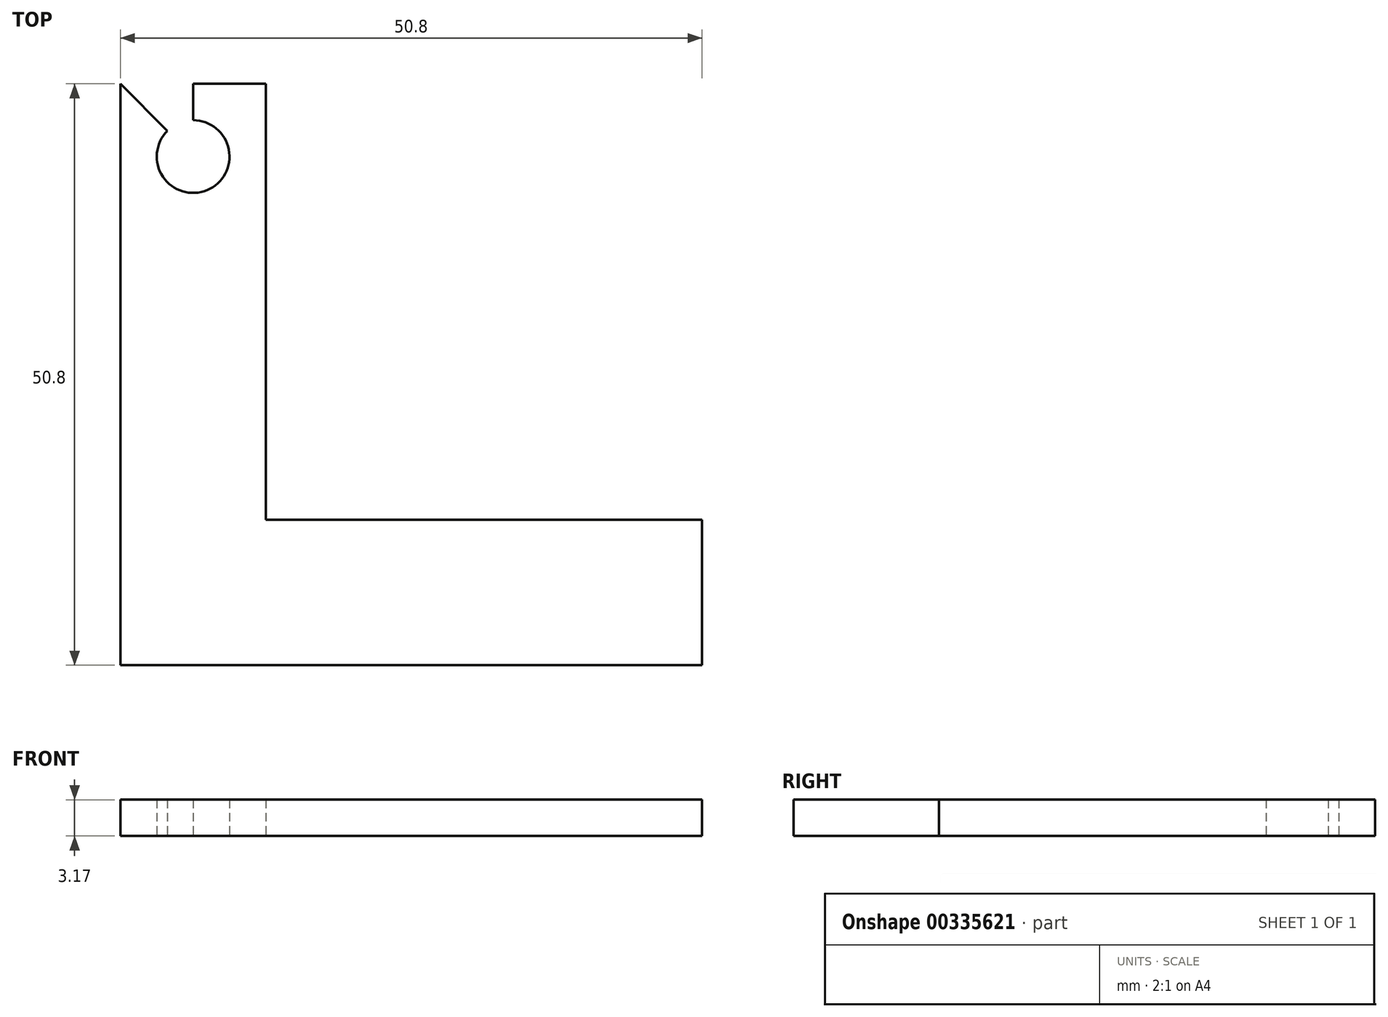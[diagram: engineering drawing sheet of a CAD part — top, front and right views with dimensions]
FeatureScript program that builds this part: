
annotation { "Feature Type Name" : "Feature", "Feature Type Description" : "" }
export const myFeature = defineFeature(function(context is Context, id is Id, definition is map)
    precondition{}
    {
        {
            var Q0;
            Q0=qCreatedBy(makeId("Top.planeOp"),FACE);
            var sketch = newSketch(context, id + "F0", { "sketchPlane" : qUnion([Q0])});
            skLineSegment(sketch, "E0.bottom", {"start": v(0, 50.8) * mm, "end": v(12.7, 50.8) * mm});
            skLineSegment(sketch, "E0.top", {"start": v(0, 0) * mm, "end": v(12.7, 0) * mm});
            skLineSegment(sketch, "E0.left", {"start": v(0, 50.8) * mm, "end": v(0, 0) * mm});
            skLineSegment(sketch, "E0.right", {"start": v(12.7, 50.8) * mm, "end": v(12.7, 0) * mm});
            skLineSegment(sketch, "E1.bottom", {"start": v(12.7, 0) * mm, "end": v(50.8, 0) * mm});
            skLineSegment(sketch, "E1.top", {"start": v(12.7, 12.7) * mm, "end": v(50.8, 12.7) * mm});
            skLineSegment(sketch, "E1.left", {"start": v(12.7, 0) * mm, "end": v(12.7, 12.7) * mm});
            skLineSegment(sketch, "E1.right", {"start": v(50.8, 0) * mm, "end": v(50.8, 12.7) * mm});
            skLineSegment(sketch, "E2.bottom", {"start": v(50.8, 12.7) * mm, "end": v(38.1, 12.7) * mm});
            skLineSegment(sketch, "E2.top", {"start": v(50.8, 25.4) * mm, "end": v(38.1, 25.4) * mm});
            skLineSegment(sketch, "E2.left", {"start": v(50.8, 12.7) * mm, "end": v(50.8, 25.4) * mm});
            skLineSegment(sketch, "E2.right", {"start": v(38.1, 12.7) * mm, "end": v(38.1, 25.4) * mm});
            skLineSegment(sketch, "E3", {"start": v(0, 50.8) * mm, "end": v(60.58, -9.78) * mm});
            skCircle(sketch, "E4", {"center": v(6.35, 44.45) * mm, "radius": 3.18 * mm});
            skLineSegment(sketch, "E5", {"start": v(6.35, 50.8) * mm, "end": v(6.35, 44.45) * mm});
            skSolve(sketch);
        }
        {
            var Q0;
            Q0=makeQuery(id+"F0.imprint","IMPRINT",FACE,{"disambiguationData":[TD([[makeQuery(id+"F0.imprint","IMPRINT",EDGE,{"derivedFrom":sQuery(id+"F0.wireOp",EDGE,"E2.bottom")}),-1.0]])]});
            var Q1;
            {var subQ0=sQuery(id+"F0.wireOp",EDGE,"E1.right");Q1=makeQuery(id+"F0.imprint","IMPRINT",FACE,{"disambiguationData":[TD([[makeQuery(id+"F0.imprint","IMPRINT",EDGE,{"derivedFrom":subQ0}),1.0]])]});}
            var Q2;
            {var subQ0=sQuery(id+"F0.wireOp",EDGE,"E1.bottom");Q2=makeQuery(id+"F0.imprint","IMPRINT",FACE,{"disambiguationData":[TD([[makeQuery(id+"F0.imprint","IMPRINT",EDGE,{"derivedFrom":subQ0}),1.0]])]});}
            var Q3;
            Q3=makeQuery(id+"F0.imprint","IMPRINT",FACE,{"disambiguationData":[TD([[makeQuery(id+"F0.imprint","IMPRINT",EDGE,{"derivedFrom":sQuery(id+"F0.wireOp",EDGE,"E0.top")}),1.0]])]});
            var Q4;
            {var subQ5=sQuery(id+"F0.wireOp",EDGE,"E0.right");var subQ7=sQuery(id+"F0.wireOp",EDGE,"E0.bottom");var subQ8=makeQuery(id+"F0.imprint","INTERSECT",VERTEX,{"derivedFrom":[subQ7,subQ5]});Q4=makeQuery(id+"F0.imprint","IMPRINT",FACE,{"disambiguationData":[TD([[makeQuery(id+"F0.imprint","IMPRINT",EDGE,{"disambiguationData":[TD([[subQ8,1.0]])],"derivedFrom":subQ7}),-1.0]])]});}
            var Q5;
            {var subQ0=sQuery(id+"F0.wireOp",EDGE,"E3");var subQ5=sQuery(id+"F0.wireOp",EDGE,"E4");var subQ6=makeQuery(id+"F0.imprint","INTERSECT",VERTEX,{"disambiguationData":[OD(0.0)],"derivedFrom":[subQ0,subQ5]});Q5=makeQuery(id+"F0.imprint","IMPRINT",FACE,{"disambiguationData":[TD([[makeQuery(id+"F0.imprint","IMPRINT",EDGE,{"disambiguationData":[TD([[subQ6,1.0]])],"derivedFrom":subQ5}),-1.0]])]});}
            extrude(context, id + "F1", {"entities" : qUnion([Q0, Q1, Q2, Q3, Q4, Q5]), "depth" : 3.17 * mm});
        }
    });
